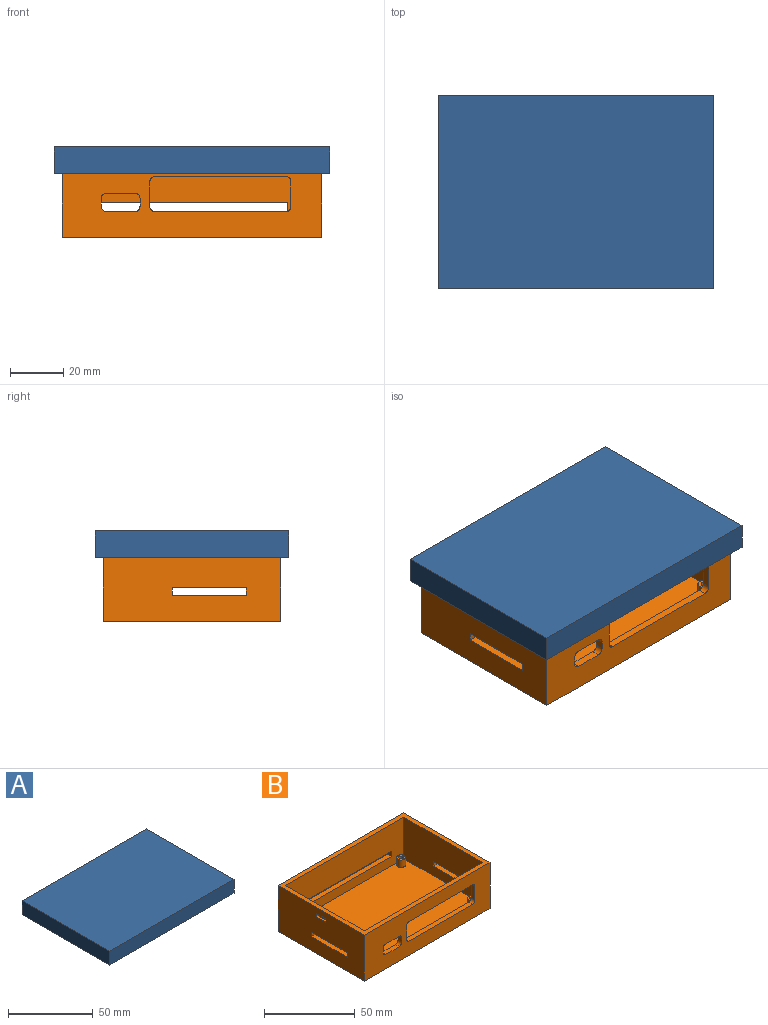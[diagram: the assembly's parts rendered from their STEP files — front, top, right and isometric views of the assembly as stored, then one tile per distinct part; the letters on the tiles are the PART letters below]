
ASSEMBLY  parts=2 mates=1
PART A: 25 faces, bbox 104x73x10 mm
  f0: plane 104x73mm, normal (0,0,-1), area 1026mm2, adj f1,f2,f3,f4,f6,f7,f8,f9
  f1: plane 104x10mm, normal (0,1,0), area 1040mm2, adj f0,f2,f4,f5
  f2: plane 73x10mm, normal (-1,0,0), area 730mm2, adj f0,f1,f3,f5
  f3: plane 104x10mm, normal (0,-1,0), area 1040mm2, adj f0,f2,f4,f5
  f4: plane 73x10mm, normal (1,0,0), area 730mm2, adj f0,f1,f3,f5
  f5: plane 104x73mm, normal (0,0,1), area 7592mm2, adj f1,f2,f3,f4
  f6: plane 98x7mm, normal (0,-1,0), area 686mm2, adj f0,f7,f9,f10
  f7: plane 67x7mm, normal (1,0,0), area 455mm2, adj f0,f6,f8,f10,f18,f19,f20,f21
  f8: plane 98x7mm, normal (0,1,0), area 686mm2, adj f0,f7,f9,f10
  f9: plane 67x7mm, normal (-1,0,0), area 455mm2, adj f0,f6,f8,f10,f11,f12,f13,f14
  f10: plane 98x67mm, normal (0,0,-1), area 6566mm2, adj f6,f7,f8,f9
  f11: plane 7x0.9mm, normal (0,0,1), area 6.3mm2, adj f9,f12,f14,f16
  f12: plane 2x1.5mm, normal (0,1,0), area 2.6mm2, adj f9,f11,f13,f15,f16,f17
  f13: plane 7x0.9mm, normal (0,0,-1), area 6.3mm2, adj f9,f12,f14,f17
  f14: plane 2x1.5mm, normal (0,-1,0), area 2.6mm2, adj f9,f11,f13,f15,f16,f17
  f15: plane 7x0.8mm, normal (-1,0,0), area 5.6mm2, adj f12,f14,f16,f17
  f16: plane 7x0.6mm, normal (-0.71,0,0.71), area 5.9mm2, adj f11,f12,f14,f15
  f17: plane 7x0.6mm, normal (-0.71,0,-0.71), area 5.9mm2, adj f12,f13,f14,f15
  f18: plane 2x1.5mm, normal (0,1,0), area 2.6mm2, adj f7,f19,f21,f22,f23,f24
  f19: plane 7x0.9mm, normal (0,0,1), area 6.3mm2, adj f7,f18,f20,f23
  f20: plane 2x1.5mm, normal (0,-1,0), area 2.6mm2, adj f7,f19,f21,f22,f23,f24
  f21: plane 7x0.9mm, normal (0,0,-1), area 6.3mm2, adj f7,f18,f20,f24
  f22: plane 7x0.8mm, normal (1,0,0), area 5.6mm2, adj f18,f20,f23,f24
  f23: plane 7x0.6mm, normal (0.71,0,0.71), area 5.9mm2, adj f18,f19,f20,f22
  f24: plane 7x0.6mm, normal (0.71,0,-0.71), area 5.9mm2, adj f18,f20,f21,f22
PART B: 65 faces, bbox 98x67x31 mm
  f0: plane 67x31mm, normal (1,0,0), area 1979mm2, adj f2,f6,f8,f9,f43,f44,f45,f46
  f1: plane 67x31mm, normal (-1,0,0), area 1977.6mm2, adj f2,f6,f8,f9,f47,f48,f49,f50
  f2: plane 98x31mm, normal (0,1,0), area 2779mm2, adj f0,f1,f8,f9,f51,f52,f53,f54
  f3: plane 92x28mm, normal (0,-1,0), area 2317mm2, adj f4,f5,f8,f10,f51,f52,f53,f54
  f4: plane 61x28mm, normal (1,0,0), area 1624mm2, adj f3,f7,f8,f10,f47,f48,f49,f50
  f5: plane 61x28mm, normal (-1,0,0), area 1624mm2, adj f3,f7,f8,f10,f43,f44,f45,f46
  f6: plane 98x31mm, normal (0,-1,0), area 2240.4mm2, adj f0,f1,f8,f9,f27,f28,f29,f30
  f7: plane 92x28mm, normal (0,1,0), area 1778.4mm2, adj f4,f5,f8,f10,f27,f28,f29,f30
  f8: plane 98x67mm, normal (0,0,1), area 954mm2, adj f0,f1,f2,f3,f4,f5,f6,f7
  f9: plane 98x67mm, normal (0,0,-1), area 6566mm2, adj f0,f1,f2,f6
  f10: plane 92x61mm, normal (0,0,1), area 5533.5mm2, adj f3,f4,f5,f7,f11,f13,f15,f17
  f11: cylinder r=2.5mm len=5mm, axis (0,0,-1), area 78.5mm2, adj f10,f12
  f12: plane 5x5mm, normal (0,0,1), area 14.7mm2, adj f11,f19
  f13: cylinder r=2.5mm len=5mm, axis (0,0,-1), area 78.5mm2, adj f10,f14
  f14: plane 5x5mm, normal (0,0,1), area 14.7mm2, adj f13,f25
  f15: cylinder r=2.5mm len=5mm, axis (0,0,-1), area 78.5mm2, adj f10,f16
  f16: plane 5x5mm, normal (0,0,1), area 14.7mm2, adj f15,f23
  f17: cylinder r=2.5mm len=5mm, axis (0,0,-1), area 78.5mm2, adj f10,f18
  f18: plane 5x5mm, normal (0,0,1), area 14.7mm2, adj f17,f21
  f19: cylinder r=1.25mm len=4mm, axis (0,0,1), area 31.4mm2, adj f12,f20
  f20: plane 2.5x2.5mm, normal (0,0,1), area 4.9mm2, adj f19
  f21: cylinder r=1.25mm len=4mm, axis (0,0,1), area 31.4mm2, adj f18,f22
  f22: plane 2.5x2.5mm, normal (0,0,1), area 4.9mm2, adj f21
  f23: cylinder r=1.25mm len=4mm, axis (0,0,1), area 31.4mm2, adj f16,f24
  f24: plane 2.5x2.5mm, normal (0,0,1), area 4.9mm2, adj f23
  f25: cylinder r=1.25mm len=4mm, axis (0,0,1), area 31.4mm2, adj f14,f26
  f26: plane 2.5x2.5mm, normal (0,0,1), area 4.9mm2, adj f25
  f27: plane 49.2x3mm, normal (0,0,-1), area 147.6mm2, adj f6,f7,f31,f34
  f28: plane 9.2x3mm, normal (1,0,0), area 27.6mm2, adj f6,f7,f31,f32
  f29: plane 49.2x3mm, normal (0,0,1), area 147.6mm2, adj f6,f7,f32,f33
  f30: plane 9.2x3mm, normal (-1,0,0), area 27.6mm2, adj f6,f7,f33,f34
  f31: cylinder r=2mm len=3mm, axis (0,-1,0), area 9.4mm2, adj f6,f7,f27,f28
  f32: cylinder r=2mm len=3mm, axis (0,1,0), area 9.4mm2, adj f6,f7,f28,f29
  f33: cylinder r=2mm len=3mm, axis (0,-1,0), area 9.4mm2, adj f6,f7,f29,f30
  f34: cylinder r=2mm len=3mm, axis (0,1,0), area 9.4mm2, adj f6,f7,f27,f30
  f35: plane 10.6x3mm, normal (0,0,-1), area 31.8mm2, adj f6,f7,f39,f42
  f36: plane 3x3mm, normal (1,0,0), area 9mm2, adj f6,f7,f39,f40
  f37: plane 10.6x3mm, normal (0,0,1), area 31.8mm2, adj f6,f7,f40,f41
  f38: plane 3x3mm, normal (-1,0,0), area 9mm2, adj f6,f7,f41,f42
  f39: cylinder r=2mm len=3mm, axis (0,-1,0), area 9.4mm2, adj f6,f7,f35,f36
  f40: cylinder r=2mm len=3mm, axis (0,1,0), area 9.4mm2, adj f6,f7,f36,f37
  f41: cylinder r=2mm len=3mm, axis (0,-1,0), area 9.4mm2, adj f6,f7,f37,f38
  f42: cylinder r=2mm len=3mm, axis (0,1,0), area 9.4mm2, adj f6,f7,f35,f38
  f43: plane 3x3mm, normal (0,1,0), area 9mm2, adj f0,f5,f44,f46
  f44: plane 28x3mm, normal (0,0,1), area 84mm2, adj f0,f5,f43,f45
  f45: plane 3x3mm, normal (0,-1,0), area 9mm2, adj f0,f5,f44,f46
  f46: plane 28x3mm, normal (0,0,-1), area 84mm2, adj f0,f5,f43,f45
  f47: plane 28x3mm, normal (0,0,-1), area 84mm2, adj f1,f4,f48,f50
  f48: plane 3x3mm, normal (0,-1,0), area 9mm2, adj f1,f4,f47,f49
  f49: plane 28x3mm, normal (0,0,1), area 84mm2, adj f1,f4,f48,f50
  f50: plane 3x3mm, normal (0,1,0), area 9mm2, adj f1,f4,f47,f49
  f51: plane 74x3mm, normal (0,0,-1), area 222mm2, adj f2,f3,f52,f54
  f52: plane 3.5x3mm, normal (-1,0,0), area 10.5mm2, adj f2,f3,f51,f53
  f53: plane 74x3mm, normal (0,0,1), area 222mm2, adj f2,f3,f52,f54
  f54: plane 3.5x3mm, normal (1,0,0), area 10.5mm2, adj f2,f3,f51,f53
  f55: plane 2.2x1.5mm, normal (0,1,0), area 3.3mm2, adj f1,f56,f58,f59
  f56: plane 7x1.5mm, normal (0,0,-1), area 10.5mm2, adj f1,f55,f57,f59
  f57: plane 2.2x1.5mm, normal (0,-1,0), area 3.3mm2, adj f1,f56,f58,f59
  f58: plane 7x1.5mm, normal (0,0,1), area 10.5mm2, adj f1,f55,f57,f59
  f59: plane 7x2.2mm, normal (-1,0,0), area 15.4mm2, adj f55,f56,f57,f58
  f60: plane 7x1.5mm, normal (0,0,-1), area 10.5mm2, adj f0,f61,f63,f64
  f61: plane 2x1.5mm, normal (0,1,0), area 3mm2, adj f0,f60,f62,f64
  f62: plane 7x1.5mm, normal (0,0,1), area 10.5mm2, adj f0,f61,f63,f64
  f63: plane 2x1.5mm, normal (0,-1,0), area 3mm2, adj f0,f60,f62,f64
  f64: plane 7x2mm, normal (1,0,0), area 14mm2, adj f60,f61,f62,f63
PLACE A t=(-11.81,-7.43,18.06)mm
PLACE B t=(-14.51,5.68,-5.94)mm
MATE fastened A.f10 <-> B.f8  axis (0,0,1) through (-62.86,-35.13,25.06)mm
